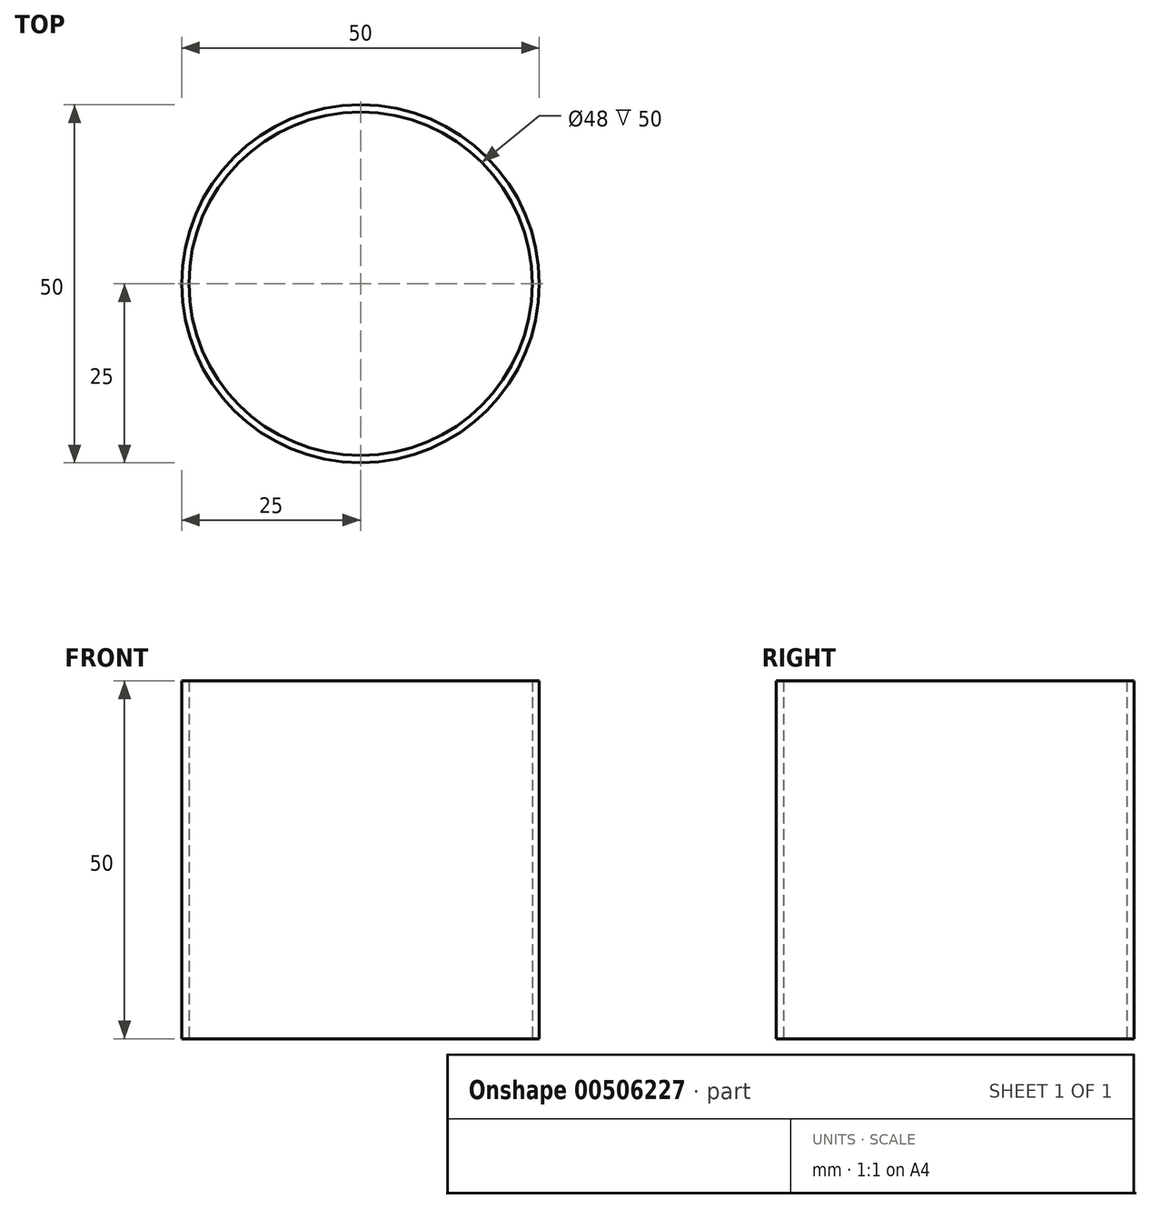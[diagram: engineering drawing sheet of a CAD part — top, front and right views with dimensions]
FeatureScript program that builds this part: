
annotation { "Feature Type Name" : "Feature", "Feature Type Description" : "" }
export const myFeature = defineFeature(function(context is Context, id is Id, definition is map)
    precondition{}
    {
        {
            var Q0;
            Q0=qCreatedBy(makeId("Top.planeOp"),FACE);
            var sketch = newSketch(context, id + "F0", { "sketchPlane" : qUnion([Q0])});
            skCircle(sketch, "E0", {"center": v(0, 0) * mm, "radius": 25 * mm});
            skCircle(sketch, "E1", {"center": v(0, 0) * mm, "radius": 24 * mm});
            skSolve(sketch);
        }
        {
            var Q0;
            Q0=makeQuery(id+"F0.imprint","IMPRINT",FACE,{"disambiguationData":[TD([[makeQuery(id+"F0.imprint","IMPRINT",EDGE,{"derivedFrom":sQuery(id+"F0.wireOp",EDGE,"E0")}),1.0]])]});
            extrude(context, id + "F1", {"entities" : qUnion([Q0]), "depth" : 50 * mm});
        }
    });
